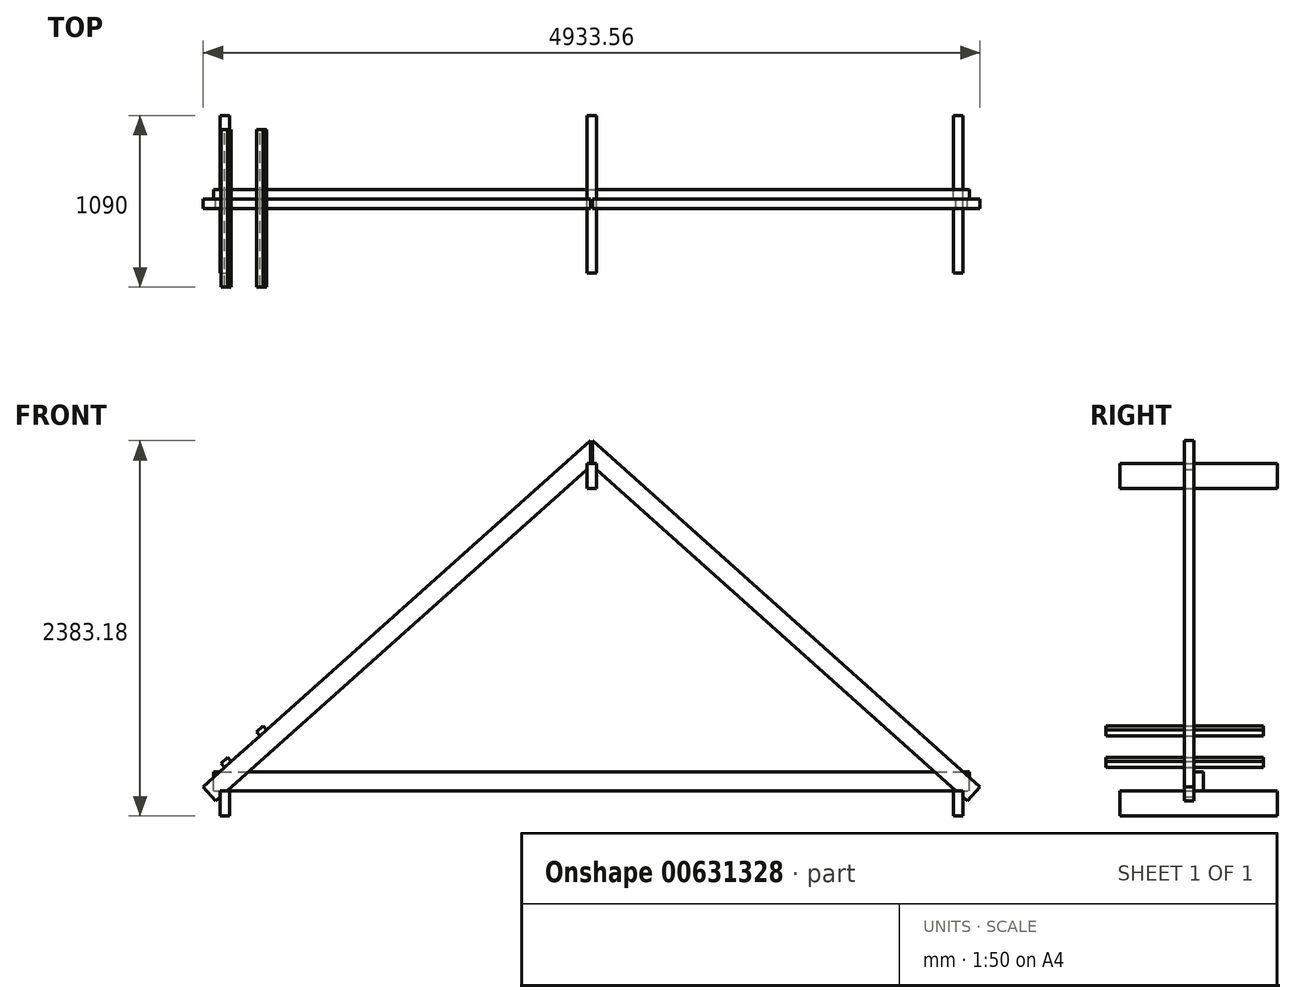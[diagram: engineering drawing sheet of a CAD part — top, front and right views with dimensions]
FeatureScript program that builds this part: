
annotation { "Feature Type Name" : "Feature", "Feature Type Description" : "" }
export const myFeature = defineFeature(function(context is Context, id is Id, definition is map)
    precondition{}
    {
        {
            var Q0;
            Q0=qCreatedBy(makeId("Front.planeOp"),FACE);
            var sketch = newSketch(context, id + "F0", { "sketchPlane" : qUnion([Q0])});
            skLineSegment(sketch, "E0.bottom", {"start": v(-2400, 0) * mm, "end": v(2400, 0) * mm});
            skLineSegment(sketch, "E0.top", {"start": v(-2400, 120) * mm, "end": v(2400, 120) * mm});
            skLineSegment(sketch, "E0.left", {"start": v(-2400, 0) * mm, "end": v(-2400, 120) * mm});
            skLineSegment(sketch, "E0.right", {"start": v(2400, 0) * mm, "end": v(2400, 120) * mm});
            skLineSegment(sketch, "E1", {"start": v(0, 0) * mm, "end": v(0, 120) * mm, "construction": true});
            skSolve(sketch);
        }
        {
            var Q0;
            Q0 = qSketchRegion(id + "F0", true);
            extrude(context, id + "F1", {"entities" : qUnion([Q0]), "endBound" : BoundingType.SYMMETRIC, "depth" : 60 * mm, "offsetDistance" : 25 * mm});
        }
        {
            var Q0;
            Q0=qCreatedBy(makeId("Front.planeOp"),FACE);
            var sketch = newSketch(context, id + "F2", { "sketchPlane" : qUnion([Q0])});
            skLineSegment(sketch, "E2.bottom", {"start": v(-2360, 0) * mm, "end": v(-2300, 0) * mm});
            skLineSegment(sketch, "E2.top", {"start": v(-2360, -160) * mm, "end": v(-2300, -160) * mm});
            skLineSegment(sketch, "E2.left", {"start": v(-2360, 0) * mm, "end": v(-2360, -160) * mm});
            skLineSegment(sketch, "E2.right", {"start": v(-2300, 0) * mm, "end": v(-2300, -160) * mm});
            skLineSegment(sketch, "E3.bottom", {"start": v(2300, 0) * mm, "end": v(2360, 0) * mm});
            skLineSegment(sketch, "E3.top", {"start": v(2300, -160) * mm, "end": v(2360, -160) * mm});
            skLineSegment(sketch, "E3.left", {"start": v(2300, 0) * mm, "end": v(2300, -160) * mm});
            skLineSegment(sketch, "E3.right", {"start": v(2360, 0) * mm, "end": v(2360, -160) * mm});
            skLineSegment(sketch, "E4", {"start": v(0, -192.14) * mm, "end": v(0, 2659.76) * mm, "construction": true});
            skLineSegment(sketch, "E5.bottom", {"start": v(-30, 2080) * mm, "end": v(30, 2080) * mm});
            skLineSegment(sketch, "E5.top", {"start": v(-30, 1920) * mm, "end": v(30, 1920) * mm});
            skLineSegment(sketch, "E5.left", {"start": v(-30, 2080) * mm, "end": v(-30, 1920) * mm});
            skLineSegment(sketch, "E5.right", {"start": v(30, 2080) * mm, "end": v(30, 1920) * mm});
            skSolve(sketch);
        }
        {
            var Q0;
            Q0 = qSketchRegion(id + "F2", true);
            extrude(context, id + "F3", {"entities" : qUnion([Q0]), "endBound" : BoundingType.SYMMETRIC, "depth" : 1000 * mm, "offsetDistance" : 25 * mm});
        }
        {
            var Q0;
            Q0=makeQuery(id+"F1.opExtrude","CAP_FACE",FACE,{"disambiguationData":[OSD([sQuery(id+"F0.wireOp",EDGE,"E0.bottom"),sQuery(id+"F0.wireOp",EDGE,"E0.top"),sQuery(id+"F0.wireOp",EDGE,"E0.left"),sQuery(id+"F0.wireOp",EDGE,"E0.right")])],"isStart":false});
            var sketch = newSketch(context, id + "F4", { "sketchPlane" : qUnion([Q0])});
            skLineSegment(sketch, "E6", {"start": v(0, -281.47) * mm, "end": v(0, 2499.3) * mm, "construction": true});
            skLineSegment(sketch, "E7", {"start": v(-5, 2080) * mm, "end": v(-30, 2080) * mm});
            skLineSegment(sketch, "E8", {"start": v(-5, 2080) * mm, "end": v(-5, 2223.18) * mm});
            skLineSegment(sketch, "E9", {"start": v(-5, 2223.18) * mm, "end": v(-2466.78, 25.53) * mm});
            skLineSegment(sketch, "E10", {"start": v(-30, 2080) * mm, "end": v(-30, 2040) * mm});
            skLineSegment(sketch, "E11", {"start": v(-30, 2040) * mm, "end": v(-2315.2, 0) * mm});
            skLineSegment(sketch, "E12", {"start": v(-2466.78, 25.53) * mm, "end": v(-2386.87, -63.98) * mm});
            skLineSegment(sketch, "E13", {"start": v(-2360, -40) * mm, "end": v(-2360, 0) * mm});
            skLineSegment(sketch, "E14", {"start": v(-2360, 0) * mm, "end": v(-2315.2, 0) * mm});
            skLineSegment(sketch, "E15.trimOffspring", {"start": v(-2360, -40) * mm, "end": v(-2386.87, -63.98) * mm});
            skLineSegment(sketch, "E16.MirrorCS", {"start": v(2360, -40) * mm, "end": v(2360, 0) * mm});
            skLineSegment(sketch, "E17.MirrorCS", {"start": v(2360, 0) * mm, "end": v(2315.2, 0) * mm});
            skLineSegment(sketch, "E18.MirrorCS", {"start": v(30, 2080) * mm, "end": v(30, 2040) * mm});
            skLineSegment(sketch, "E19.MirrorCS", {"start": v(5, 2080) * mm, "end": v(30, 2080) * mm});
            skLineSegment(sketch, "E20.MirrorCS", {"start": v(2360, -40) * mm, "end": v(2386.87, -63.98) * mm});
            skLineSegment(sketch, "E21.MirrorCS", {"start": v(2466.78, 25.53) * mm, "end": v(2386.87, -63.98) * mm});
            skLineSegment(sketch, "E22.MirrorCS", {"start": v(5, 2080) * mm, "end": v(5, 2223.18) * mm});
            skLineSegment(sketch, "E23.MirrorCS", {"start": v(30, 2040) * mm, "end": v(2315.2, 0) * mm});
            skLineSegment(sketch, "E24.MirrorCS", {"start": v(5, 2223.18) * mm, "end": v(2466.78, 25.53) * mm});
            skSolve(sketch);
        }
        {
            var Q0;
            Q0 = qSketchRegion(id + "F4", true);
            extrude(context, id + "F5", {"entities" : qUnion([Q0]), "depth" : 60 * mm, "offsetDistance" : 25 * mm});
        }
        {
            var Q0;
            Q0=makeQuery(id+"F5.opExtrude","CAP_FACE",FACE,{"disambiguationData":[OSD([sQuery(id+"F4.wireOp",EDGE,"E7"),sQuery(id+"F4.wireOp",EDGE,"E8"),sQuery(id+"F4.wireOp",EDGE,"E9"),sQuery(id+"F4.wireOp",EDGE,"E10"),sQuery(id+"F4.wireOp",EDGE,"E11"),sQuery(id+"F4.wireOp",EDGE,"E12"),sQuery(id+"F4.wireOp",EDGE,"E13"),sQuery(id+"F4.wireOp",EDGE,"E14"),sQuery(id+"F4.wireOp",EDGE,"E15.trimOffspring")])],"isStart":false});
            var sketch = newSketch(context, id + "F6", { "sketchPlane" : qUnion([Q0])});
            skLineSegment(sketch, "E25", {"start": v(-2287.93, 185.2) * mm, "end": v(-2311.24, 211.3) * mm});
            skLineSegment(sketch, "E26", {"start": v(-2311.24, 211.3) * mm, "end": v(-2352.27, 174.68) * mm});
            skLineSegment(sketch, "E27", {"start": v(-2352.27, 174.68) * mm, "end": v(-2328.96, 148.57) * mm});
            skLineSegment(sketch, "E28", {"start": v(-2328.96, 148.57) * mm, "end": v(-2287.93, 185.2) * mm});
            skLineSegment(sketch, "E29", {"start": v(-2105.17, 348.35) * mm, "end": v(-2128.47, 374.46) * mm});
            skLineSegment(sketch, "E30", {"start": v(-2128.47, 374.46) * mm, "end": v(-2087.44, 411.09) * mm});
            skLineSegment(sketch, "E31", {"start": v(-2087.44, 411.09) * mm, "end": v(-2064.14, 384.98) * mm});
            skLineSegment(sketch, "E32", {"start": v(-2064.14, 384.98) * mm, "end": v(-2105.17, 348.35) * mm});
            skSolve(sketch);
        }
        {
            var Q0;
            Q0 = qSketchRegion(id + "F6", true);
            extrude(context, id + "F7", {"entities" : qUnion([Q0]), "operationType" : NewBodyOperationType.ADD, "endBound" : BoundingType.SYMMETRIC, "depth" : 1000 * mm, "offsetDistance" : 25 * mm});
        }
    });
